FCSTD DOCUMENT  (FreeCAD 1.0R38806 (Git))
Label: Opgave_3.0.3
License: All rights reserved
LicenseURL: http://en.wikipedia.org/wiki/All_rights_reserved
objects: Sketcher::SketchObject×3, App::VarSet×1, PartDesign::Body×1, App::Part×1
note: 7 computed .brp shape members not serialized (recipe doc carries the construction recipe); baked Part::Feature solids carry a one-line shape summary decoded from their .brp

FEATURE [App::VarSet] VarSet
  BasePlateGridX = 2
  BasePlateGridY = 3
  BasePlateProfileAngle = 45
  BasePlateProfileHeigth = 4.65
  BasePlateProfileLower = 0.7
  BasePlateProfileMiddle = 1.8
  BasePlateProfileTop = 2.15
  BaseplatePad2nd_Length = 0.4
  BaseplatePadLength = 3
  GridOuterRadius = 4
  GridSize = 42
  expr: BasePlateProfileHeigth = BasePlateProfileLower + BasePlateProfileMiddle + BasePlateProfileTop
FEATURE [Sketcher::SketchObject] Sketch
  ArcFitTolerance = 1e-06
  AttachmentSupport = -> [XY_Plane001]
  FullyConstrained = false
  MakeInternals = false
  MapMode = 5
  sketch-geometry (4):
    g0: LineSegment StartX=-22.4848 StartY=-26.9697 StartZ=0 EndX=22.4848 EndY=-26.9697 EndZ=0
    g1: LineSegment StartX=22.4848 StartY=-26.9697 StartZ=0 EndX=22.4848 EndY=26.9697 EndZ=0
    g2: LineSegment StartX=22.4848 StartY=26.9697 StartZ=0 EndX=-22.4848 EndY=26.9697 EndZ=0
    g3: LineSegment StartX=-22.4848 StartY=26.9697 StartZ=0 EndX=-22.4848 EndY=-26.9697 EndZ=0
  constraints (8):
    c: Coincident(g0,g1)
    c: Coincident(g1,g2)
    c: Coincident(g2,g3)
    c: Coincident(g3,g0)
    c: Horizontal(g0)
    c: Horizontal(g2)
    c: Vertical(g1)
    c: Vertical(g3)
FEATURE [Sketcher::SketchObject] Sketch001
  ArcFitTolerance = 1e-06
  AttachmentSupport = -> [XY_Plane001]
  FullyConstrained = false
  MakeInternals = false
  MapMode = 5
  sketch-geometry (10):
    g0: LineSegment StartX=-6.32398 StartY=-18.9705 StartZ=0 EndX=6.32398 EndY=-18.9705 EndZ=0
    g1: LineSegment StartX=12.8081 StartY=-12.4864 StartZ=0 EndX=12.8081 EndY=12.4864 EndZ=0
    g2: LineSegment StartX=6.32398 StartY=18.9705 StartZ=0 EndX=-6.32398 EndY=18.9705 EndZ=0
    g3: LineSegment StartX=-12.8081 StartY=12.4864 StartZ=0 EndX=-12.8081 EndY=-12.4864 EndZ=0
    g4: ArcOfCircle CenterX=-6.32398 CenterY=-12.4864 CenterZ=0 NormalX=0 NormalY=0 NormalZ=1 AngleXU=0 Radius=6.48415 StartAngle=3.14159 EndAngle=4.71239
    g5: ArcOfCircle CenterX=6.32398 CenterY=-12.4864 CenterZ=0 NormalX=0 NormalY=0 NormalZ=1 AngleXU=0 Radius=6.48415 StartAngle=4.71239 EndAngle=6.28319
    g6: ArcOfCircle CenterX=6.32398 CenterY=12.4864 CenterZ=0 NormalX=0 NormalY=0 NormalZ=1 AngleXU=0 Radius=6.48415 StartAngle=0 EndAngle=1.5708
    g7: ArcOfCircle CenterX=-6.32398 CenterY=12.4864 CenterZ=0 NormalX=0 NormalY=0 NormalZ=1 AngleXU=0 Radius=6.48415 StartAngle=1.5708 EndAngle=3.14159
    g8: GeomPoint [constr] X=12.8081 Y=18.9705 Z=0
    g9: GeomPoint [constr] X=0 Y=0 Z=0
  constraints (19):
    c: Tangent(g0,g4) = -1.5708
    c: Tangent(g0,g5) = -1.5708
    c: Tangent(g1,g5) = -1.5708
    c: Tangent(g1,g6) = -1.5708
    c: Tangent(g2,g6) = -1.5708
    c: Tangent(g2,g7) = -1.5708
    c: Tangent(g3,g7) = -1.5708
    c: Tangent(g3,g4) = -1.5708
    c: Horizontal(g0)
    c: Horizontal(g2)
    c: Vertical(g1)
    c: Vertical(g3)
    c: Equal(g4,g5)
    c: Equal(g5,g6)
    c: Equal(g6,g7)
    c: Symmetric(g2,g0,g9)
    c: PointOnObject(g8,g1)
    c: PointOnObject(g8,g2)
    c: Coincident(g9,g-1)
FEATURE [Sketcher::SketchObject] Sketch002
  ArcFitTolerance = 1e-06
  AttachmentSupport = -> [XZ_Plane001]
  FullyConstrained = false
  MakeInternals = false
  MapMode = 5
  Placement = pos=(0,0,0) rot=(1,0,0;1.5708rad)
  sketch-geometry (5):
    g0: LineSegment StartX=21.8575 StartY=8.34358 StartZ=0 EndX=20.1836 EndY=6.6996 EndZ=0
    g1: LineSegment StartX=20.1836 StartY=6.6996 StartZ=0 EndX=20.1836 EndY=4.33824 EndZ=0
    g2: LineSegment StartX=20.1836 StartY=4.33824 StartZ=0 EndX=18.8385 EndY=3.02306 EndZ=0
    g3: LineSegment StartX=18.8385 StartY=3.02306 StartZ=0 EndX=18.8385 EndY=8.34358 EndZ=0
    g4: LineSegment StartX=18.8385 StartY=8.34358 StartZ=0 EndX=21.8575 EndY=8.34358 EndZ=0
  constraints (8):
    c: Coincident(g0,g1)
    c: Vertical(g1)
    c: Coincident(g1,g2)
    c: Coincident(g2,g3)
    c: Vertical(g3)
    c: Coincident(g3,g4)
    c: Coincident(g4,g0)
    c: Horizontal(g4)
FEATURE [PartDesign::Body] Body  label="Baseplate"
  AllowCompound = true
  Group = -> [Sketch,Sketch001,Sketch002]
  Origin = -> Origin001
FEATURE [App::Part] Part
  Group = -> [Body]
  Origin = -> Origin
